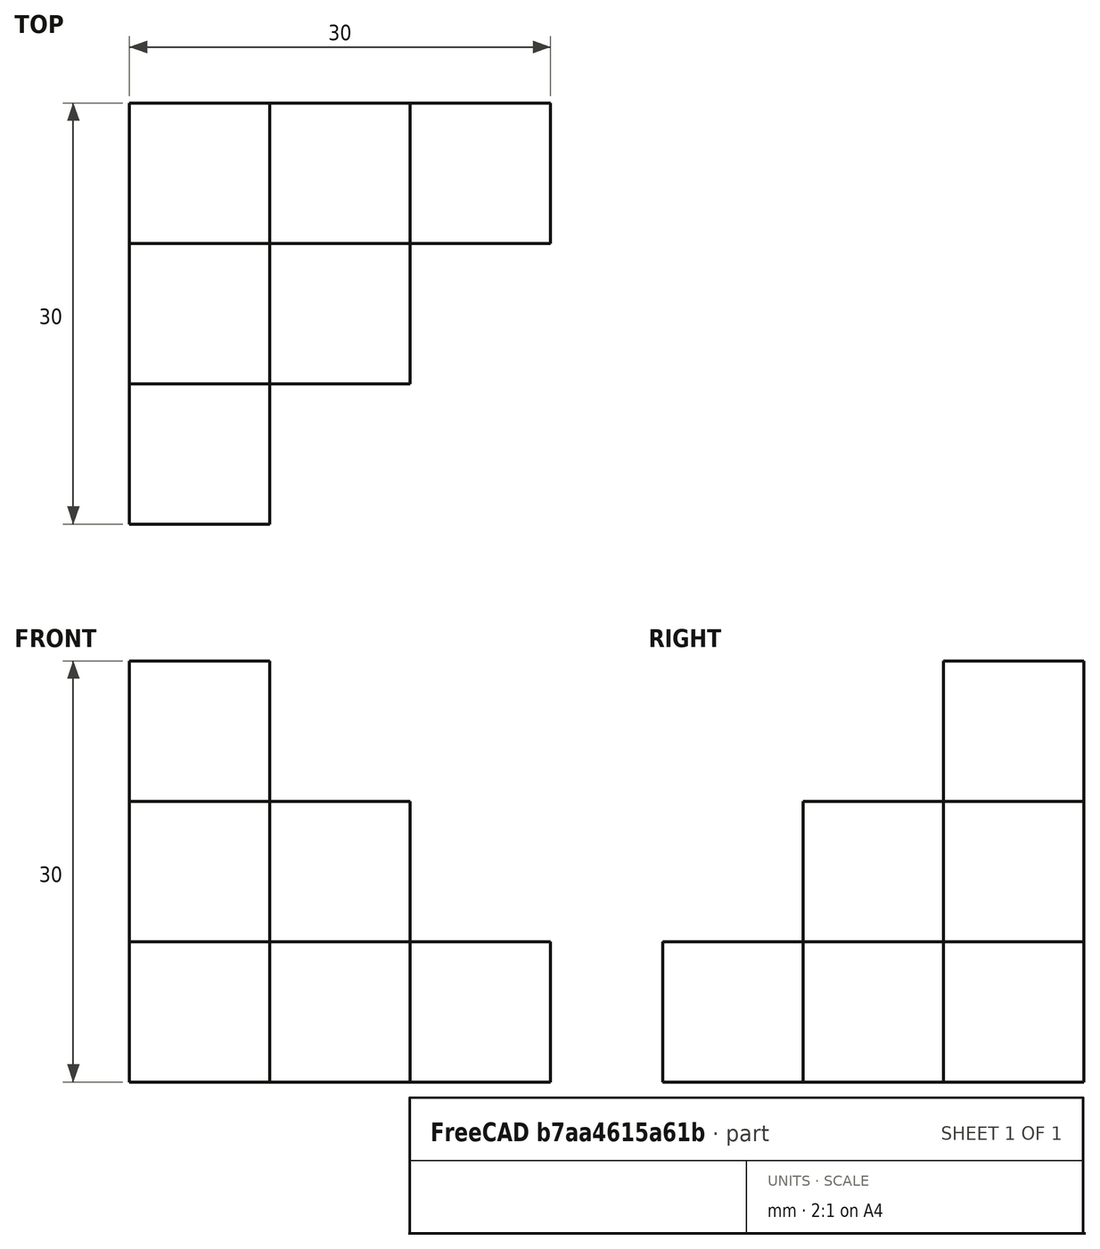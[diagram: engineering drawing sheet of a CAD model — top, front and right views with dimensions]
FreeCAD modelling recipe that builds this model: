
FCSTD DOCUMENT  (FreeCAD 1.0R39319 (Git))
Label: ojt1_t05r02_refine shapes
License: All rights reserved
LicenseURL: https://en.wikipedia.org/wiki/All_rights_reserved
objects: Part::Box×6, Part::MultiFuse×1
note: 7 computed .brp shape members not serialized (recipe doc carries the construction recipe); baked Part::Feature solids carry a one-line shape summary decoded from their .brp

FEATURE [Part::Box] Box  label="Cube"
  AttacherType = Attacher::AttachEngine3D
  Height = 30
  Length = 10
  Width = 10
FEATURE [Part::Box] Box001  label="Cube001"
  AttacherType = Attacher::AttachEngine3D
  Height = 20
  Length = 10
  Placement = pos=(10,0,0) rot=(0,0,1;0rad)
  Width = 10
FEATURE [Part::Box] Box002  label="Cube002"
  AttacherType = Attacher::AttachEngine3D
  Height = 20
  Length = 10
  Placement = pos=(0,-10,0) rot=(0,0,1;0rad)
  Width = 10
FEATURE [Part::Box] Box003  label="Cube003"
  AttacherType = Attacher::AttachEngine3D
  Height = 10
  Length = 10
  Placement = pos=(10,-10,0) rot=(0,0,1;0rad)
  Width = 10
FEATURE [Part::Box] Box004  label="Cube004"
  AttacherType = Attacher::AttachEngine3D
  Height = 10
  Length = 10
  Placement = pos=(0,-20,0) rot=(0,0,1;0rad)
  Width = 10
FEATURE [Part::Box] Box005  label="Cube005"
  AttacherType = Attacher::AttachEngine3D
  Height = 10
  Length = 10
  Placement = pos=(20,0,0) rot=(0,0,1;0rad)
  Width = 10
FEATURE [Part::MultiFuse] Fusion
  Refine = true
  Shapes = -> [Box,Box001,Box002,Box003,Box004,Box005]
